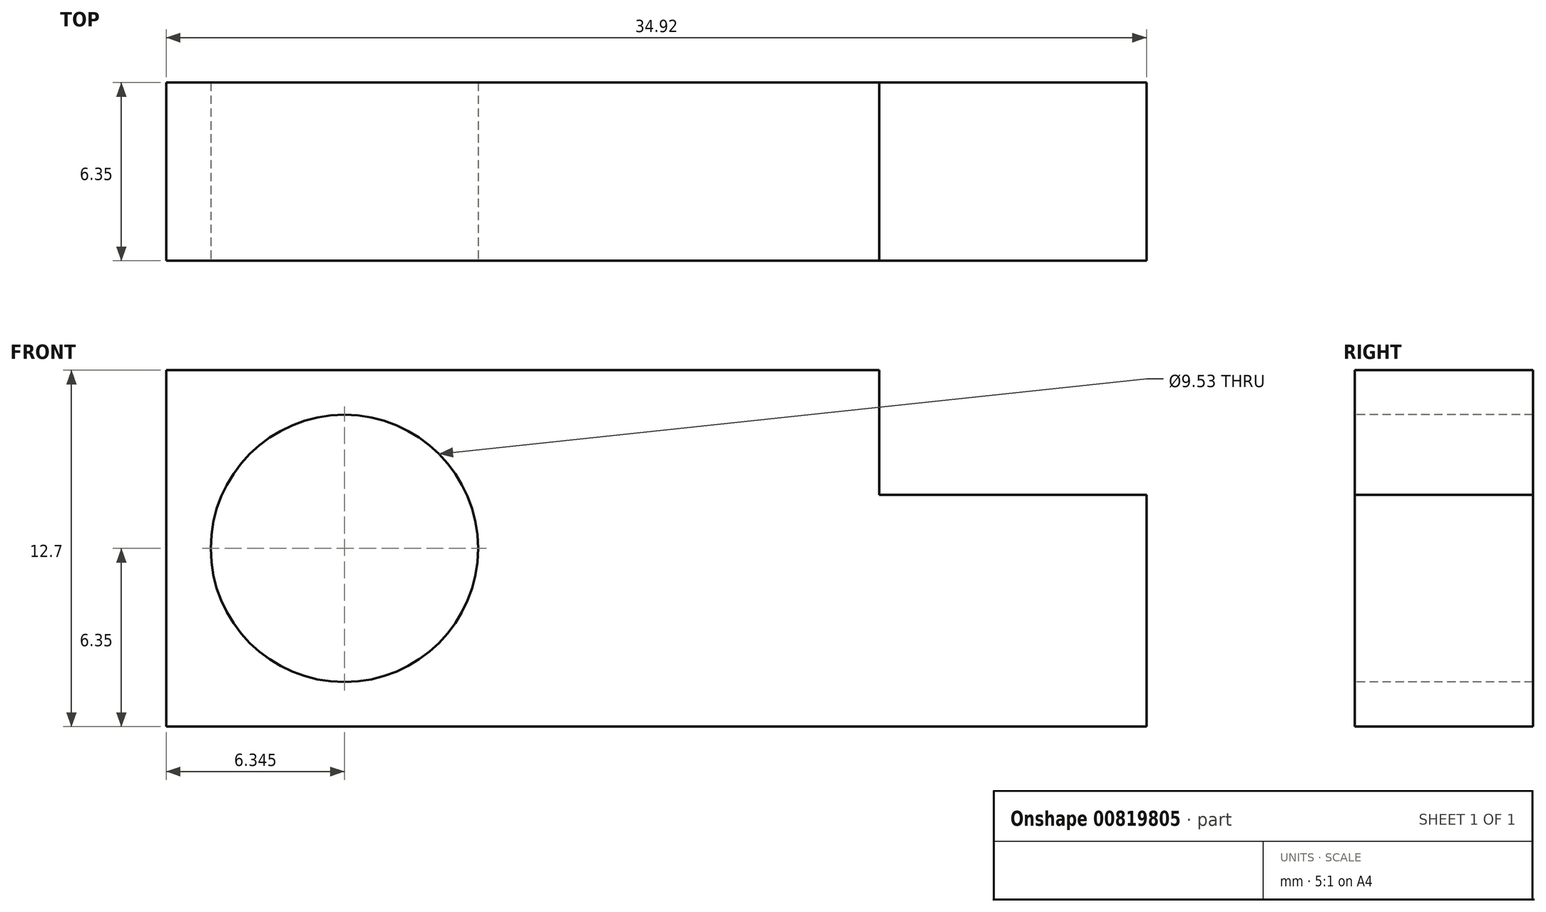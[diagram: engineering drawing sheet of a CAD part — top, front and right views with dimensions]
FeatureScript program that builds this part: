
annotation { "Feature Type Name" : "Feature", "Feature Type Description" : "" }
export const myFeature = defineFeature(function(context is Context, id is Id, definition is map)
    precondition{}
    {
        {
            var Q0;
            Q0=qCreatedBy(makeId("Front.planeOp"),FACE);
            var sketch = newSketch(context, id + "F0", { "sketchPlane" : qUnion([Q0])});
            skLineSegment(sketch, "E0", {"start": v(0, 0) * mm, "end": v(-34.93, 0) * mm});
            skLineSegment(sketch, "E1", {"start": v(-34.93, 0) * mm, "end": v(-34.93, 12.7) * mm});
            skLineSegment(sketch, "E2", {"start": v(-34.93, 12.7) * mm, "end": v(-9.53, 12.7) * mm});
            skLineSegment(sketch, "E3", {"start": v(-9.53, 12.7) * mm, "end": v(-9.53, 8.25) * mm});
            skLineSegment(sketch, "E4", {"start": v(-9.53, 8.25) * mm, "end": v(0, 8.26) * mm});
            skLineSegment(sketch, "E5", {"start": v(0, 8.26) * mm, "end": v(0, 0) * mm});
            skCircle(sketch, "E6", {"center": v(-28.58, 6.35) * mm, "radius": 4.76 * mm});
            skSolve(sketch);
        }
        {
            var Q0;
            Q0=makeQuery(id+"F0.imprint","IMPRINT",FACE,{"disambiguationData":[TD([[makeQuery(id+"F0.imprint","IMPRINT",EDGE,{"derivedFrom":sQuery(id+"F0.wireOp",EDGE,"E0")}),-1.0]])]});
            extrude(context, id + "F1", {"entities" : qUnion([Q0]), "oppositeDirection" : true, "depth" : 6.35 * mm, "offsetDistance" : 25.4 * mm});
        }
    });
